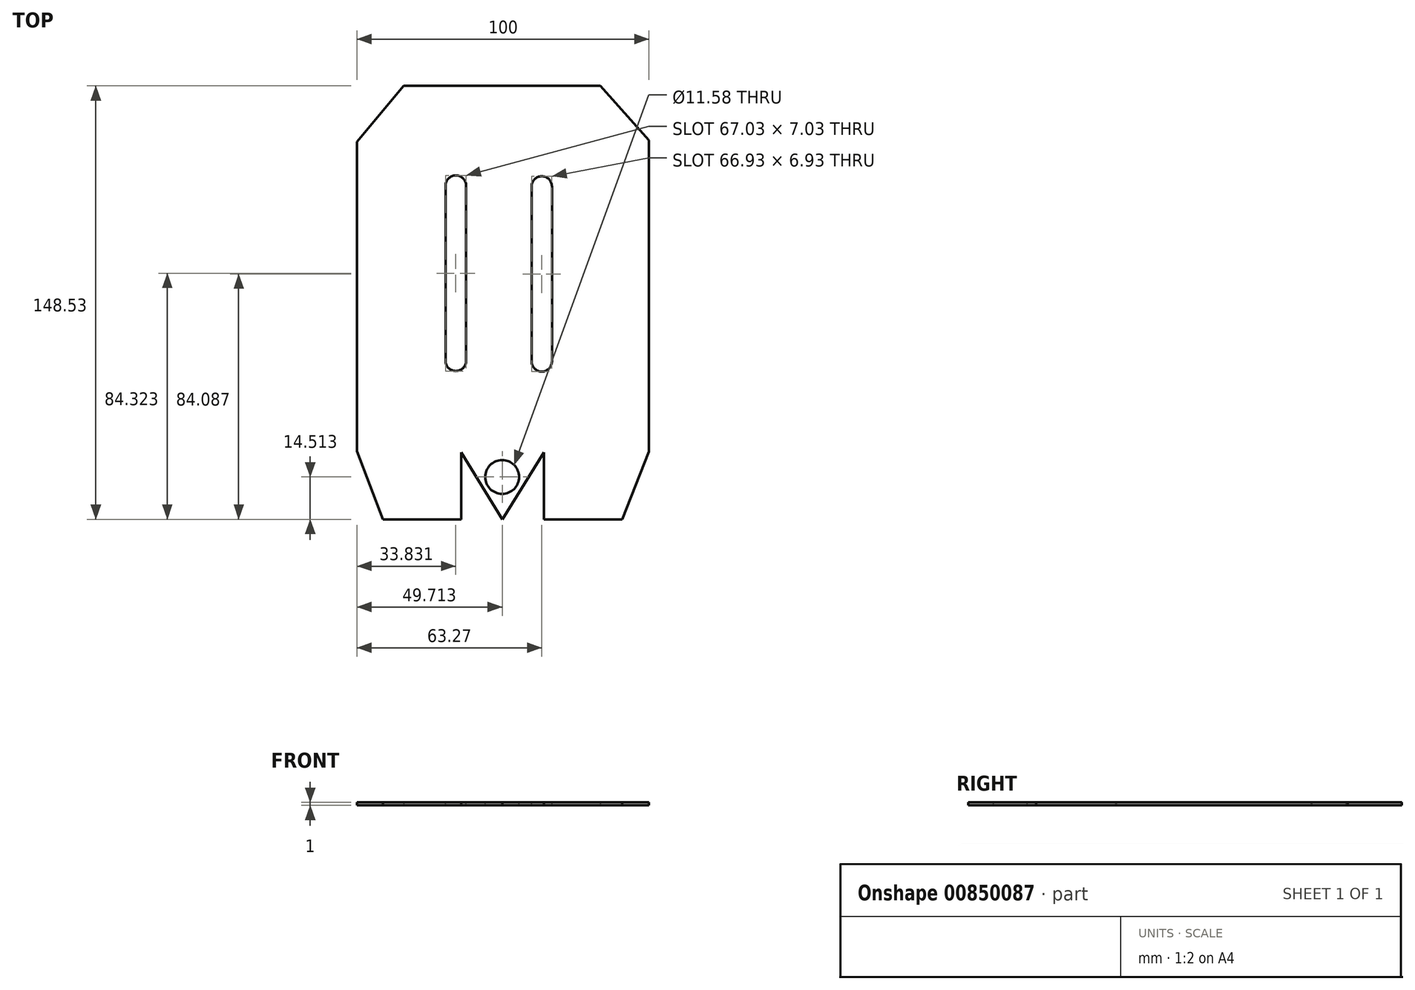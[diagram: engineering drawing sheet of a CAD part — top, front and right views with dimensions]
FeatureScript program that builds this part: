
annotation { "Feature Type Name" : "Feature", "Feature Type Description" : "" }
export const myFeature = defineFeature(function(context is Context, id is Id, definition is map)
    precondition{}
    {
        {
            var Q0;
            Q0=qCreatedBy(makeId("Top.planeOp"),FACE);
            var sketch = newSketch(context, id + "F0", { "sketchPlane" : qUnion([Q0])});
            skLineSegment(sketch, "E0.bottom", {"start": v(-27.23, 70.43) * mm, "end": v(40.07, 70.43) * mm});
            skLineSegment(sketch, "E0.top", {"start": v(-34.4, -78.1) * mm, "end": v(47.53, -78.1) * mm});
            skLineSegment(sketch, "E0.left", {"start": v(-43.25, 51.24) * mm, "end": v(-43.25, -54.71) * mm});
            skLineSegment(sketch, "E0.right", {"start": v(56.75, 51.8) * mm, "end": v(56.75, -54.86) * mm});
            skLineSegment(sketch, "E1", {"start": v(-27.23, 70.43) * mm, "end": v(-43.25, 51.24) * mm});
            skLineSegment(sketch, "E2", {"start": v(40.07, 70.43) * mm, "end": v(56.75, 51.8) * mm});
            skLineSegment(sketch, "E3", {"start": v(-43.25, -54.71) * mm, "end": v(-34.4, -78.1) * mm});
            skLineSegment(sketch, "E4", {"start": v(56.75, -54.86) * mm, "end": v(47.53, -78.1) * mm});
            skLineSegment(sketch, "E5", {"start": v(-7.58, -78.1) * mm, "end": v(-7.58, -55.1) * mm});
            skLineSegment(sketch, "E6", {"start": v(-7.58, -55.1) * mm, "end": v(6.56, -78.1) * mm});
            skLineSegment(sketch, "E7", {"start": v(6.56, -78.1) * mm, "end": v(20.7, -55.1) * mm});
            skLineSegment(sketch, "E8", {"start": v(20.7, -55.1) * mm, "end": v(20.7, -78.1) * mm});
            skSolve(sketch);
        }
        {
            var Q0;
            Q0=makeQuery(id+"F0.imprint","IMPRINT",FACE,{"disambiguationData":[TD([[makeQuery(id+"F0.imprint","IMPRINT",EDGE,{"derivedFrom":sQuery(id+"F0.wireOp",EDGE,"E0.bottom")}),-1.0]])]});
            extrude(context, id + "F1", {"entities" : qUnion([Q0]), "depth" : 1 * mm, "offsetDistance" : 25 * mm});
        }
        {
            var Q0;
            Q0=makeQuery(id+"F1.opExtrude","CAP_FACE",FACE,{"disambiguationData":[OSD([sQuery(id+"F0.wireOp",EDGE,"E0.bottom"),sQuery(id+"F0.wireOp",EDGE,"E0.top"),sQuery(id+"F0.wireOp",EDGE,"E0.left"),sQuery(id+"F0.wireOp",EDGE,"E0.right"),sQuery(id+"F0.wireOp",EDGE,"E1"),sQuery(id+"F0.wireOp",EDGE,"E2"),sQuery(id+"F0.wireOp",EDGE,"E3"),sQuery(id+"F0.wireOp",EDGE,"E4"),sQuery(id+"F0.wireOp",EDGE,"E5"),sQuery(id+"F0.wireOp",EDGE,"E6"),sQuery(id+"F0.wireOp",EDGE,"E7"),sQuery(id+"F0.wireOp",EDGE,"E8")])],"isStart":false});
            var sketch = newSketch(context, id + "F2", { "sketchPlane" : qUnion([Q0])});
            skLineSegment(sketch, "E9", {"start": v(-12.94, 36.22) * mm, "end": v(-12.94, -23.78) * mm});
            skLineSegment(sketch, "E10", {"start": v(-5.9, 36.22) * mm, "end": v(-5.9, -23.78) * mm});
            skArc(sketch, "E11", {"start": v(-12.94, -23.78) * mm, "mid": v(-9.42, -27.3) * mm, "end": v(-5.9, -23.78) * mm});
            skArc(sketch, "E12", {"start": v(-5.9, 36.22) * mm, "mid": v(-9.42, 39.74) * mm, "end": v(-12.94, 36.22) * mm});
            skCircle(sketch, "E13", {"center": v(6.46, -63.59) * mm, "radius": 5.79 * mm});
            skSolve(sketch);
        }
        {
            var Q0;
            Q0=makeQuery(id+"F2.imprint","IMPRINT",FACE,{"disambiguationData":[TD([[makeQuery(id+"F2.imprint","IMPRINT",EDGE,{"derivedFrom":sQuery(id+"F2.wireOp",EDGE,"E9")}),1.0]])]});
            extrude(context, id + "F3", {"entities" : qUnion([Q0]), "operationType" : NewBodyOperationType.REMOVE, "oppositeDirection" : true, "depth" : 25 * mm, "offsetDistance" : 25 * mm});
        }
        {
            var Q0;
            Q0=makeQuery(id+"F2.imprint","IMPRINT",FACE,{"disambiguationData":[TD([[makeQuery(id+"F2.imprint","IMPRINT",EDGE,{"derivedFrom":sQuery(id+"F2.wireOp",EDGE,"E9")}),-1.0]])]});
            var sketch = newSketch(context, id + "F4", { "sketchPlane" : qUnion([Q0])});
            skLineSegment(sketch, "E14", {"start": v(16.55, -24.01) * mm, "end": v(16.55, 35.99) * mm});
            skLineSegment(sketch, "E15", {"start": v(23.48, 35.99) * mm, "end": v(23.48, -24.01) * mm});
            skArc(sketch, "E16", {"start": v(23.48, 35.99) * mm, "mid": v(20.02, 39.45) * mm, "end": v(16.55, 35.99) * mm});
            skArc(sketch, "E17", {"start": v(16.55, -24.01) * mm, "mid": v(20.02, -27.48) * mm, "end": v(23.48, -24.01) * mm});
            skSolve(sketch);
        }
        {
            var Q0;
            Q0 = qSketchRegion(id + "F4", true);
            extrude(context, id + "F5", {"entities" : qUnion([Q0]), "operationType" : NewBodyOperationType.REMOVE, "oppositeDirection" : true, "depth" : 25 * mm, "offsetDistance" : 25 * mm});
        }
        {
            var Q0;
            Q0=makeQuery(id+"F2.imprint","IMPRINT",FACE,{"disambiguationData":[TD([[makeQuery(id+"F2.imprint","IMPRINT",EDGE,{"derivedFrom":sQuery(id+"F2.wireOp",EDGE,"E9")}),1.0]])]});
            extrude(context, id + "F6", {"entities" : qUnion([Q0]), "operationType" : NewBodyOperationType.REMOVE, "oppositeDirection" : true, "depth" : 25 * mm, "offsetDistance" : 25 * mm});
        }
        {
            var Q0;
            Q0 = qSketchRegion(id + "F2", true);
            var Q1;
            Q1=makeQuery(id+"F1.opExtrude","CAP_FACE",FACE,{"disambiguationData":[OSD([sQuery(id+"F0.wireOp",EDGE,"E0.bottom"),sQuery(id+"F0.wireOp",EDGE,"E0.top"),sQuery(id+"F0.wireOp",EDGE,"E0.left"),sQuery(id+"F0.wireOp",EDGE,"E0.right"),sQuery(id+"F0.wireOp",EDGE,"E1"),sQuery(id+"F0.wireOp",EDGE,"E2"),sQuery(id+"F0.wireOp",EDGE,"E3"),sQuery(id+"F0.wireOp",EDGE,"E4"),sQuery(id+"F0.wireOp",EDGE,"E5"),sQuery(id+"F0.wireOp",EDGE,"E6"),sQuery(id+"F0.wireOp",EDGE,"E7"),sQuery(id+"F0.wireOp",EDGE,"E8")])],"isStart":true});
            extrude(context, id + "F7", {"entities" : qUnion([Q0, Q1]), "operationType" : NewBodyOperationType.REMOVE, "oppositeDirection" : true, "depth" : 25 * mm, "offsetDistance" : 25 * mm});
        }
    });
